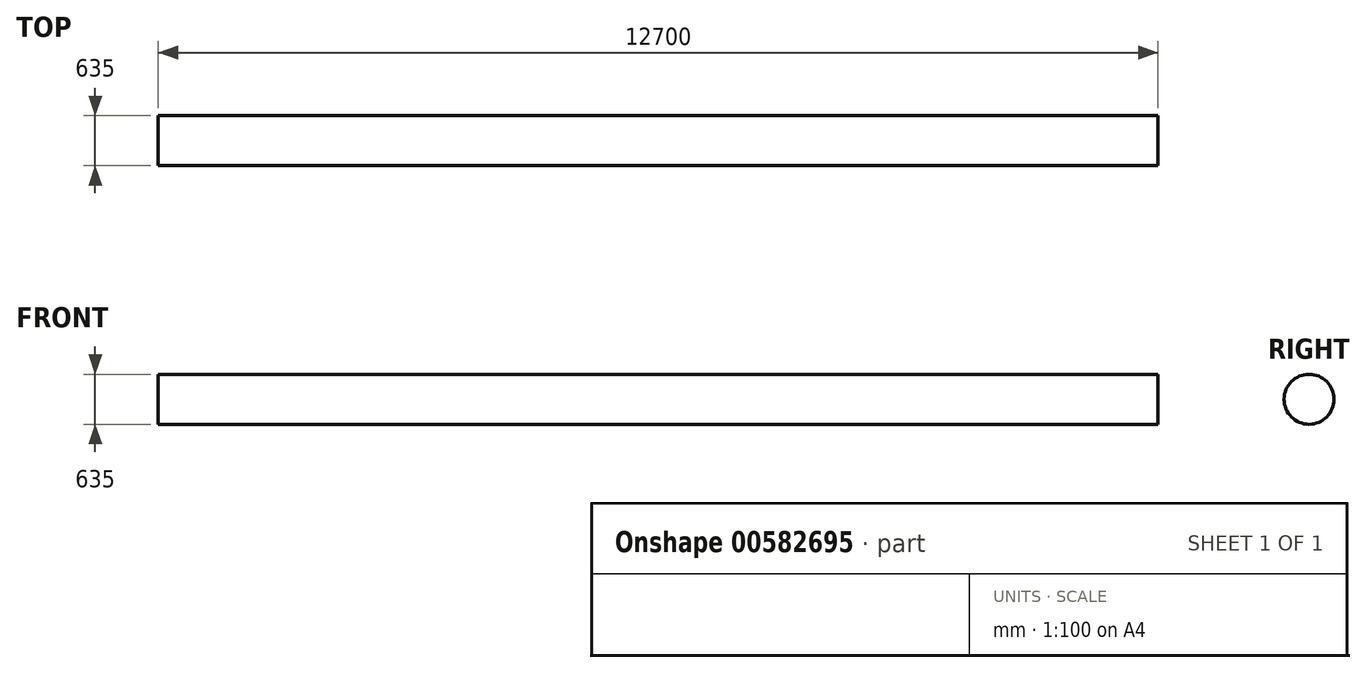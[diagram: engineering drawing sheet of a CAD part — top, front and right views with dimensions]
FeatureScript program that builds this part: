
annotation { "Feature Type Name" : "Feature", "Feature Type Description" : "" }
export const myFeature = defineFeature(function(context is Context, id is Id, definition is map)
    precondition{}
    {
        {
            var Q0;
            Q0=qCreatedBy(makeId("Right.planeOp"),FACE);
            var sketch = newSketch(context, id + "F0", { "sketchPlane" : qUnion([Q0])});
            skCircle(sketch, "E0", {"center": v(0, 0) * mm, "radius": 317.5 * mm});
            skSolve(sketch);
        }
        {
            var Q0;
            Q0 = qSketchRegion(id + "F0", true);
            extrude(context, id + "F1", {"entities" : qUnion([Q0]), "depth" : 12700 * mm, "offsetDistance" : 25.4 * mm});
        }
    });
